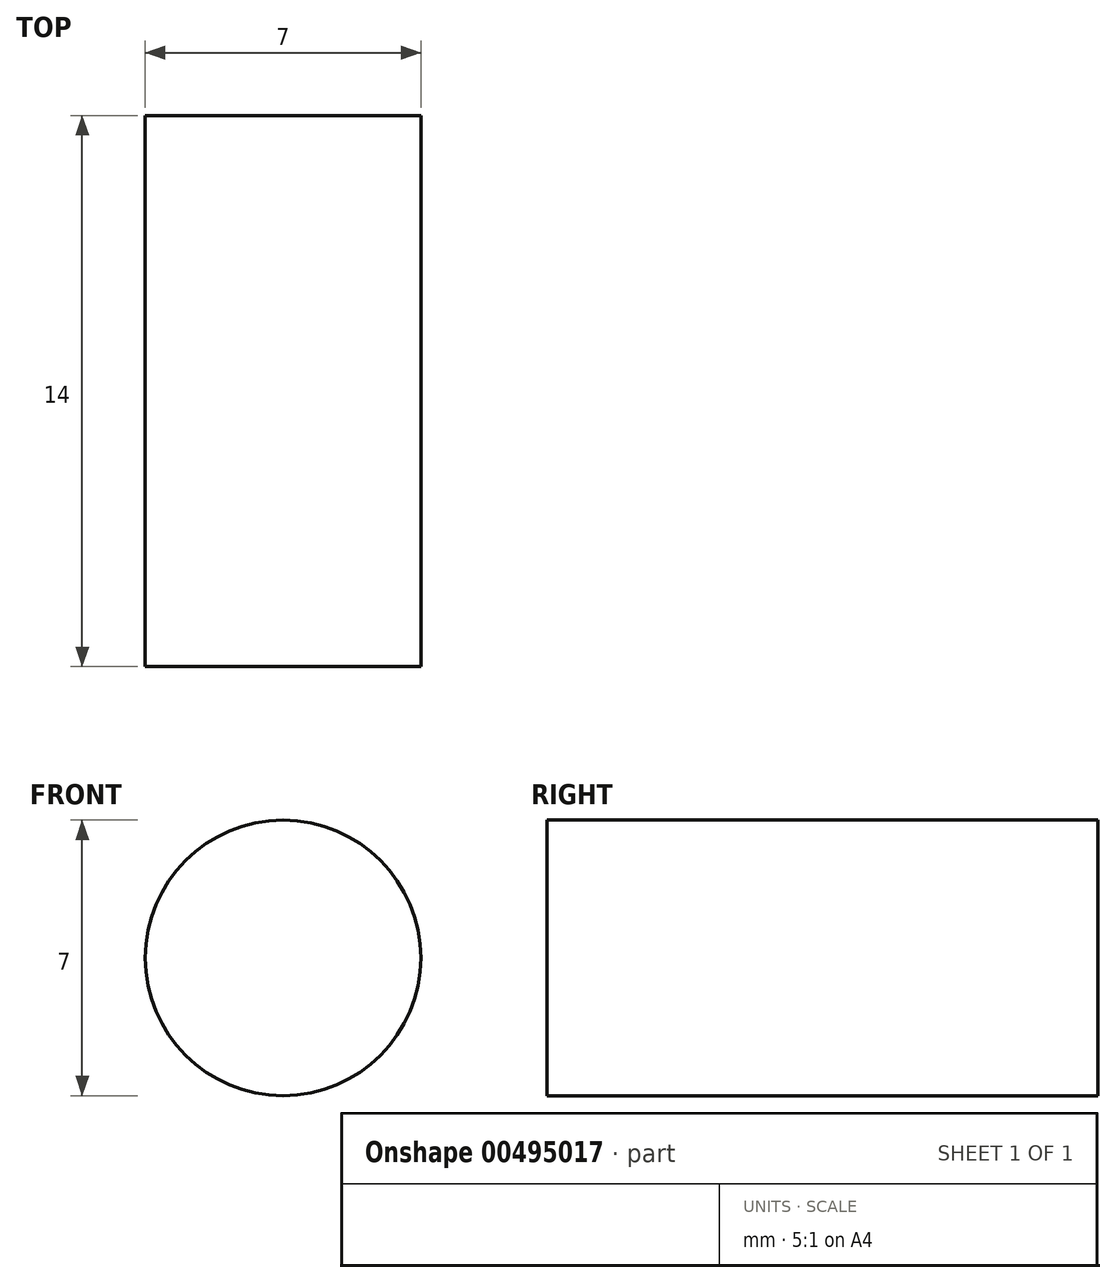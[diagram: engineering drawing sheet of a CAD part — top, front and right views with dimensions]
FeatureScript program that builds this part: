
annotation { "Feature Type Name" : "Feature", "Feature Type Description" : "" }
export const myFeature = defineFeature(function(context is Context, id is Id, definition is map)
    precondition{}
    {
        {
            var Q0;
            Q0=qCreatedBy(makeId("Front.planeOp"),FACE);
            var sketch = newSketch(context, id + "F0", { "sketchPlane" : qUnion([Q0])});
            skCircle(sketch, "E0", {"center": v(0, 0) * mm, "radius": 3.5 * mm});
            skSolve(sketch);
        }
        {
            var Q0;
            Q0=makeQuery(id+"F0.imprint","IMPRINT",FACE,{"disambiguationData":[TD([[makeQuery(id+"F0.imprint","IMPRINT",EDGE,{"derivedFrom":sQuery(id+"F0.wireOp",EDGE,"E0")}),1.0]])]});
            extrude(context, id + "F1", {"entities" : qUnion([Q0]), "depth" : 14 * mm, "offsetDistance" : 25.4 * mm});
        }
    });
